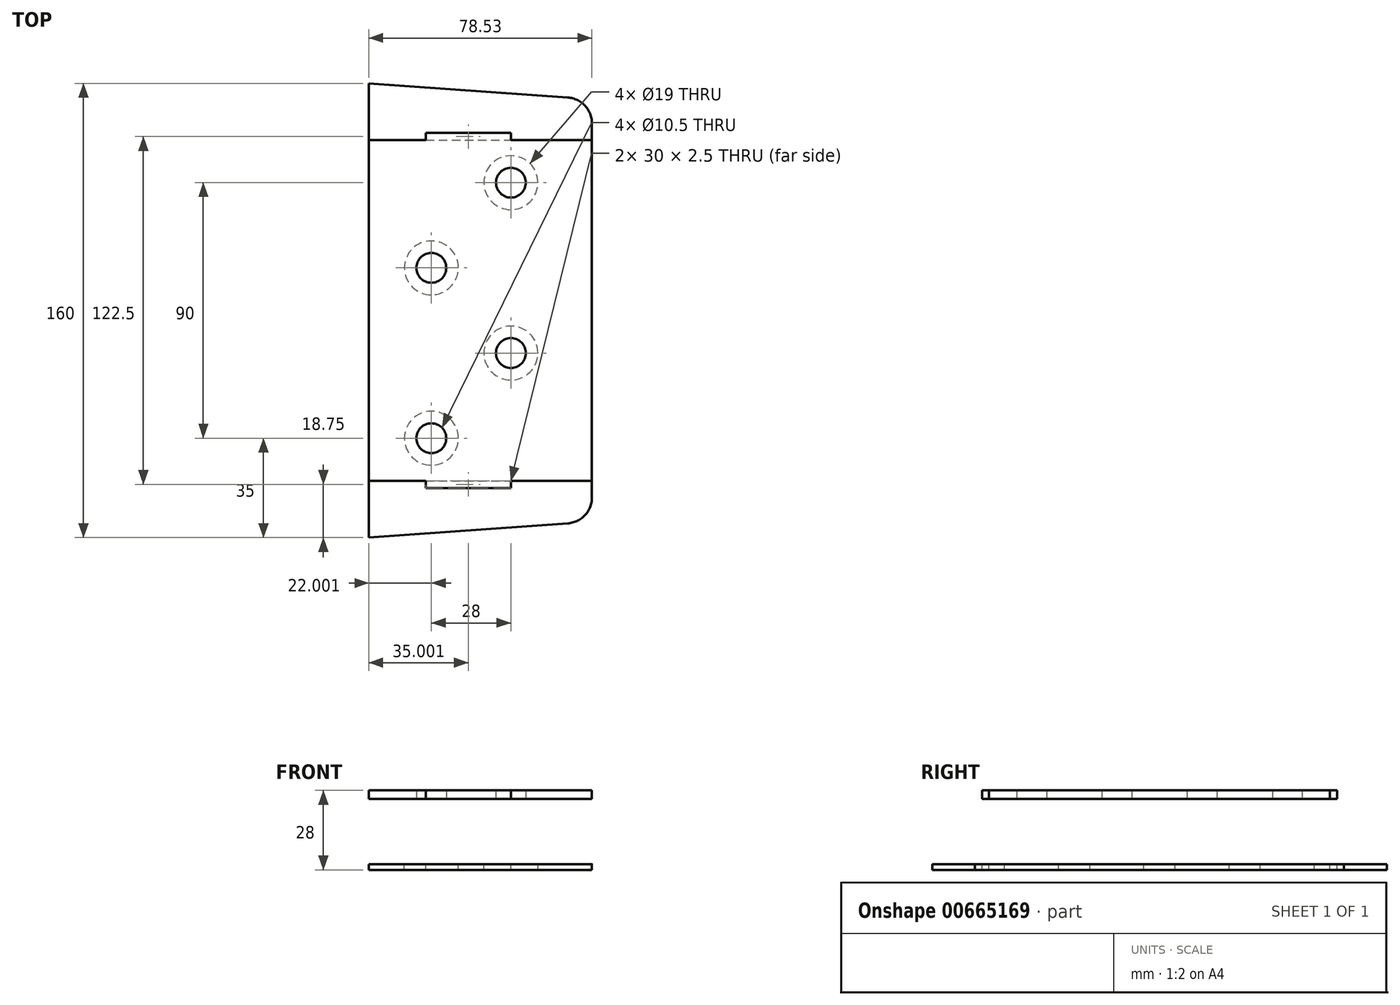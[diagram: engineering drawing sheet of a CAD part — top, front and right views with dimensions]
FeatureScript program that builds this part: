
annotation { "Feature Type Name" : "Feature", "Feature Type Description" : "" }
export const myFeature = defineFeature(function(context is Context, id is Id, definition is map)
    precondition{}
    {
        {
            var Q0;
            Q0=qCreatedBy(makeId("Top.planeOp"),FACE);
            var sketch = newSketch(context, id + "F0", { "sketchPlane" : qUnion([Q0])});
            skLineSegment(sketch, "E0", {"start": v(-42.79, 80) * mm, "end": v(-42.79, -80) * mm});
            skLineSegment(sketch, "E1", {"start": v(-42.79, 80) * mm, "end": v(27.21, 75) * mm});
            skLineSegment(sketch, "E2.MirrorCS", {"start": v(-42.79, -80) * mm, "end": v(27.21, -75) * mm});
            skLineSegment(sketch, "E3", {"start": v(35.7, 65) * mm, "end": v(35.7, -65) * mm});
            skArc(sketch, "E4", {"start": v(27.21, -75) * mm, "mid": v(33.56, -71.78) * mm, "end": v(35.7, -65) * mm});
            skArc(sketch, "E5", {"start": v(27.21, 75) * mm, "mid": v(33.56, 71.78) * mm, "end": v(35.7, 65) * mm});
            skSolve(sketch);
        }
        {
            var Q0;
            Q0=makeQuery(id+"F0.imprint","IMPRINT",FACE,{"disambiguationData":[TD([[makeQuery(id+"F0.imprint","IMPRINT",EDGE,{"derivedFrom":sQuery(id+"F0.wireOp",EDGE,"E0")}),1.0]])]});
            extrude(context, id + "F1", {"entities" : qUnion([Q0]), "depth" : 2 * mm, "offsetDistance" : 25 * mm});
        }
        {
            var Q0;
            Q0=makeQuery(id+"F1.opExtrude","CAP_FACE",FACE,{"disambiguationData":[OSD([sQuery(id+"F0.wireOp",EDGE,"E0"),sQuery(id+"F0.wireOp",EDGE,"E1"),sQuery(id+"F0.wireOp",EDGE,"E2.MirrorCS"),sQuery(id+"F0.wireOp",EDGE,"E3"),sQuery(id+"F0.wireOp",EDGE,"E4"),sQuery(id+"F0.wireOp",EDGE,"E5")])],"isStart":false});
            var sketch = newSketch(context, id + "F2", { "sketchPlane" : qUnion([Q0])});
            skLineSegment(sketch, "E6.0", {"start": v(-42.79, 80) * mm, "end": v(27.21, 75) * mm});
            skLineSegment(sketch, "E7", {"start": v(-20.79, 86.42) * mm, "end": v(-20.79, -83.07) * mm, "construction": true});
            skLineSegment(sketch, "E8", {"start": v(7.21, 84.15) * mm, "end": v(7.21, -82.57) * mm, "construction": true});
            skLineSegment(sketch, "E9", {"start": v(-83, 0) * mm, "end": v(59.47, 0) * mm, "construction": true});
            skLineSegment(sketch, "E10", {"start": v(-82.75, 15) * mm, "end": v(67.55, 15) * mm, "construction": true});
            skLineSegment(sketch, "E11", {"start": v(-78.65, 45) * mm, "end": v(63.97, 45) * mm, "construction": true});
            skCircle(sketch, "E12", {"center": v(-20.79, 15) * mm, "radius": 17.5 * mm, "construction": true});
            skCircle(sketch, "E13", {"center": v(7.21, 45) * mm, "radius": 17.5 * mm, "construction": true});
            skLineSegment(sketch, "E14", {"start": v(-82.94, -15) * mm, "end": v(62.1, -15) * mm, "construction": true});
            skLineSegment(sketch, "E15", {"start": v(-81.74, -45) * mm, "end": v(58.89, -45) * mm, "construction": true});
            skCircle(sketch, "E16", {"center": v(7.21, -15) * mm, "radius": 17.5 * mm, "construction": true});
            skCircle(sketch, "E17", {"center": v(-20.79, -45) * mm, "radius": 17.5 * mm, "construction": true});
            skCircle(sketch, "E18", {"center": v(7.21, 45) * mm, "radius": 9.5 * mm});
            skCircle(sketch, "E19", {"center": v(-20.79, 15) * mm, "radius": 9.5 * mm});
            skCircle(sketch, "E20", {"center": v(7.21, -15) * mm, "radius": 9.5 * mm});
            skCircle(sketch, "E21", {"center": v(-20.79, -45) * mm, "radius": 9.5 * mm});
            skSolve(sketch);
        }
        {
            var Q0;
            Q0=makeQuery(id+"F2.imprint","IMPRINT",FACE,{"disambiguationData":[TD([[makeQuery(id+"F2.imprint","IMPRINT",EDGE,{"derivedFrom":sQuery(id+"F2.wireOp",EDGE,"E18")}),1.0]])]});
            var Q1;
            Q1=makeQuery(id+"F2.imprint","IMPRINT",FACE,{"disambiguationData":[TD([[makeQuery(id+"F2.imprint","IMPRINT",EDGE,{"derivedFrom":sQuery(id+"F2.wireOp",EDGE,"E19")}),1.0]])]});
            var Q2;
            Q2=makeQuery(id+"F2.imprint","IMPRINT",FACE,{"disambiguationData":[TD([[makeQuery(id+"F2.imprint","IMPRINT",EDGE,{"derivedFrom":sQuery(id+"F2.wireOp",EDGE,"E20")}),1.0]])]});
            var Q3;
            Q3=makeQuery(id+"F2.imprint","IMPRINT",FACE,{"disambiguationData":[TD([[makeQuery(id+"F2.imprint","IMPRINT",EDGE,{"derivedFrom":sQuery(id+"F2.wireOp",EDGE,"E21")}),1.0]])]});
            extrude(context, id + "F3", {"entities" : qUnion([Q0, Q1, Q2, Q3]), "operationType" : NewBodyOperationType.REMOVE, "endBound" : BoundingType.UP_TO_NEXT, "oppositeDirection" : true, "depth" : 25 * mm, "offsetDistance" : 25 * mm});
        }
        {
            var Q0;
            Q0=qCreatedBy(makeId("Top.planeOp"),FACE);
            cPlane(context, id + "F4", {"entities" : qUnion([Q0]), "cplaneType" : CPlaneType.OFFSET, "offset" : 25 * mm, "width" : 150 * mm, "height" : 150 * mm});
        }
        {
            var Q0;
            Q0=qCreatedBy(id+"F4.planeOp",FACE);
            var sketch = newSketch(context, id + "F5", { "sketchPlane" : qUnion([Q0])});
            skLineSegment(sketch, "E22.0", {"start": v(-42.79, 80) * mm, "end": v(-42.79, -80) * mm});
            skPoint(sketch, "E23.0", {"position": v(-7.79, -77.5) * mm});
            skLineSegment(sketch, "E24.0", {"start": v(-42.79, -80) * mm, "end": v(27.21, -75) * mm});
            skArc(sketch, "E25.0", {"start": v(27.21, -75) * mm, "mid": v(33.56, -71.78) * mm, "end": v(35.7, -65) * mm});
            skLineSegment(sketch, "E26.0", {"start": v(35.7, 65) * mm, "end": v(35.7, -65) * mm});
            skArc(sketch, "E27.0", {"start": v(27.21, 75) * mm, "mid": v(33.56, 71.78) * mm, "end": v(35.7, 65) * mm});
            skLineSegment(sketch, "E28.0", {"start": v(-42.79, 80) * mm, "end": v(27.21, 75) * mm});
            skLineSegment(sketch, "E29", {"start": v(-59.46, 0) * mm, "end": v(63.75, 0) * mm, "construction": true});
            skCircle(sketch, "E30", {"center": v(7.21, 45) * mm, "radius": 5.25 * mm});
            skCircle(sketch, "E31", {"center": v(-20.79, 15) * mm, "radius": 5.25 * mm});
            skCircle(sketch, "E32", {"center": v(7.21, -15) * mm, "radius": 5.25 * mm});
            skCircle(sketch, "E33", {"center": v(-20.79, -45) * mm, "radius": 5.25 * mm});
            skLineSegment(sketch, "E34", {"start": v(-42.79, 60) * mm, "end": v(-22.79, 60) * mm});
            skLineSegment(sketch, "E35", {"start": v(-22.79, 60) * mm, "end": v(-22.79, 62.5) * mm});
            skLineSegment(sketch, "E36", {"start": v(-22.79, 62.5) * mm, "end": v(7.21, 62.5) * mm});
            skLineSegment(sketch, "E37", {"start": v(7.21, 62.5) * mm, "end": v(7.21, 60) * mm});
            skLineSegment(sketch, "E38", {"start": v(7.21, 60) * mm, "end": v(35.7, 60) * mm});
            skLineSegment(sketch, "E39.MirrorCS", {"start": v(-42.79, -60) * mm, "end": v(-22.79, -60) * mm});
            skLineSegment(sketch, "E40.MirrorCS", {"start": v(-22.79, -60) * mm, "end": v(-22.79, -62.5) * mm});
            skLineSegment(sketch, "E41.MirrorCS", {"start": v(-22.79, -62.5) * mm, "end": v(7.21, -62.5) * mm});
            skLineSegment(sketch, "E42.MirrorCS", {"start": v(7.21, -62.5) * mm, "end": v(7.21, -60) * mm});
            skLineSegment(sketch, "E43.MirrorCS", {"start": v(7.21, -60) * mm, "end": v(35.7, -60) * mm});
            skLineSegment(sketch, "E44", {"start": v(-42.79, 60) * mm, "end": v(-42.79, -60) * mm});
            skLineSegment(sketch, "E45", {"start": v(35.7, 60) * mm, "end": v(35.7, -60) * mm});
            skSolve(sketch);
        }
        {
            var Q0;
            Q0=makeQuery(id+"F5.imprint","IMPRINT",FACE,{"disambiguationData":[TD([[makeQuery(id+"F5.imprint","IMPRINT",EDGE,{"derivedFrom":sQuery(id+"F5.wireOp",EDGE,"E30")}),-1.0]])]});
            extrude(context, id + "F6", {"entities" : qUnion([Q0]), "depth" : 3 * mm, "offsetDistance" : 25 * mm});
        }
        {
            var Q0;
            Q0=makeQuery(id+"F1.opExtrude","CAP_FACE",FACE,{"disambiguationData":[OSD([sQuery(id+"F0.wireOp",EDGE,"E0"),sQuery(id+"F0.wireOp",EDGE,"E1"),sQuery(id+"F0.wireOp",EDGE,"E2.MirrorCS"),sQuery(id+"F0.wireOp",EDGE,"E3"),sQuery(id+"F0.wireOp",EDGE,"E4"),sQuery(id+"F0.wireOp",EDGE,"E5")])],"isStart":false});
            var sketch = newSketch(context, id + "F7", { "sketchPlane" : qUnion([Q0])});
            skLineSegment(sketch, "E46.0", {"start": v(-42.79, 60) * mm, "end": v(-22.79, 60) * mm});
            skLineSegment(sketch, "E47.0", {"start": v(-22.79, 62.5) * mm, "end": v(7.21, 62.5) * mm});
            skLineSegment(sketch, "E48.0", {"start": v(7.21, 60) * mm, "end": v(35.7, 60) * mm});
            skLineSegment(sketch, "E49.0", {"start": v(-22.79, 60) * mm, "end": v(-22.79, 62.5) * mm});
            skLineSegment(sketch, "E50.0", {"start": v(7.21, 62.5) * mm, "end": v(7.21, 60) * mm});
            skLineSegment(sketch, "E51", {"start": v(-60.63, 0) * mm, "end": v(65.58, 0) * mm, "construction": true});
            skLineSegment(sketch, "E52.bottom", {"start": v(-22.79, 60) * mm, "end": v(7.21, 60) * mm});
            skLineSegment(sketch, "E52.right", {"start": v(7.21, 60) * mm, "end": v(7.21, 62.5) * mm});
            skLineSegment(sketch, "E53.MirrorCS", {"start": v(-22.79, -62.5) * mm, "end": v(7.21, -62.5) * mm});
            skLineSegment(sketch, "E54.MirrorCS", {"start": v(7.21, -60) * mm, "end": v(7.21, -62.5) * mm});
            skLineSegment(sketch, "E55.MirrorCS", {"start": v(-22.79, -60) * mm, "end": v(-22.79, -62.5) * mm});
            skLineSegment(sketch, "E56.MirrorCS", {"start": v(-22.79, -60) * mm, "end": v(7.21, -60) * mm});
            skSolve(sketch);
        }
        {
            var Q0;
            Q0=makeQuery(id+"F7.imprint","IMPRINT",FACE,{"disambiguationData":[TD([[makeQuery(id+"F7.imprint","IMPRINT",EDGE,{"derivedFrom":sQuery(id+"F7.wireOp",EDGE,"E52.bottom")}),1.0]])]});
            var Q1;
            Q1=makeQuery(id+"F7.imprint","IMPRINT",FACE,{"disambiguationData":[TD([[makeQuery(id+"F7.imprint","IMPRINT",EDGE,{"derivedFrom":sQuery(id+"F7.wireOp",EDGE,"E53.MirrorCS")}),1.0]])]});
            extrude(context, id + "F8", {"entities" : qUnion([Q0, Q1]), "operationType" : NewBodyOperationType.REMOVE, "endBound" : BoundingType.UP_TO_NEXT, "oppositeDirection" : true, "depth" : 25 * mm, "offsetDistance" : 25 * mm});
        }
    });
